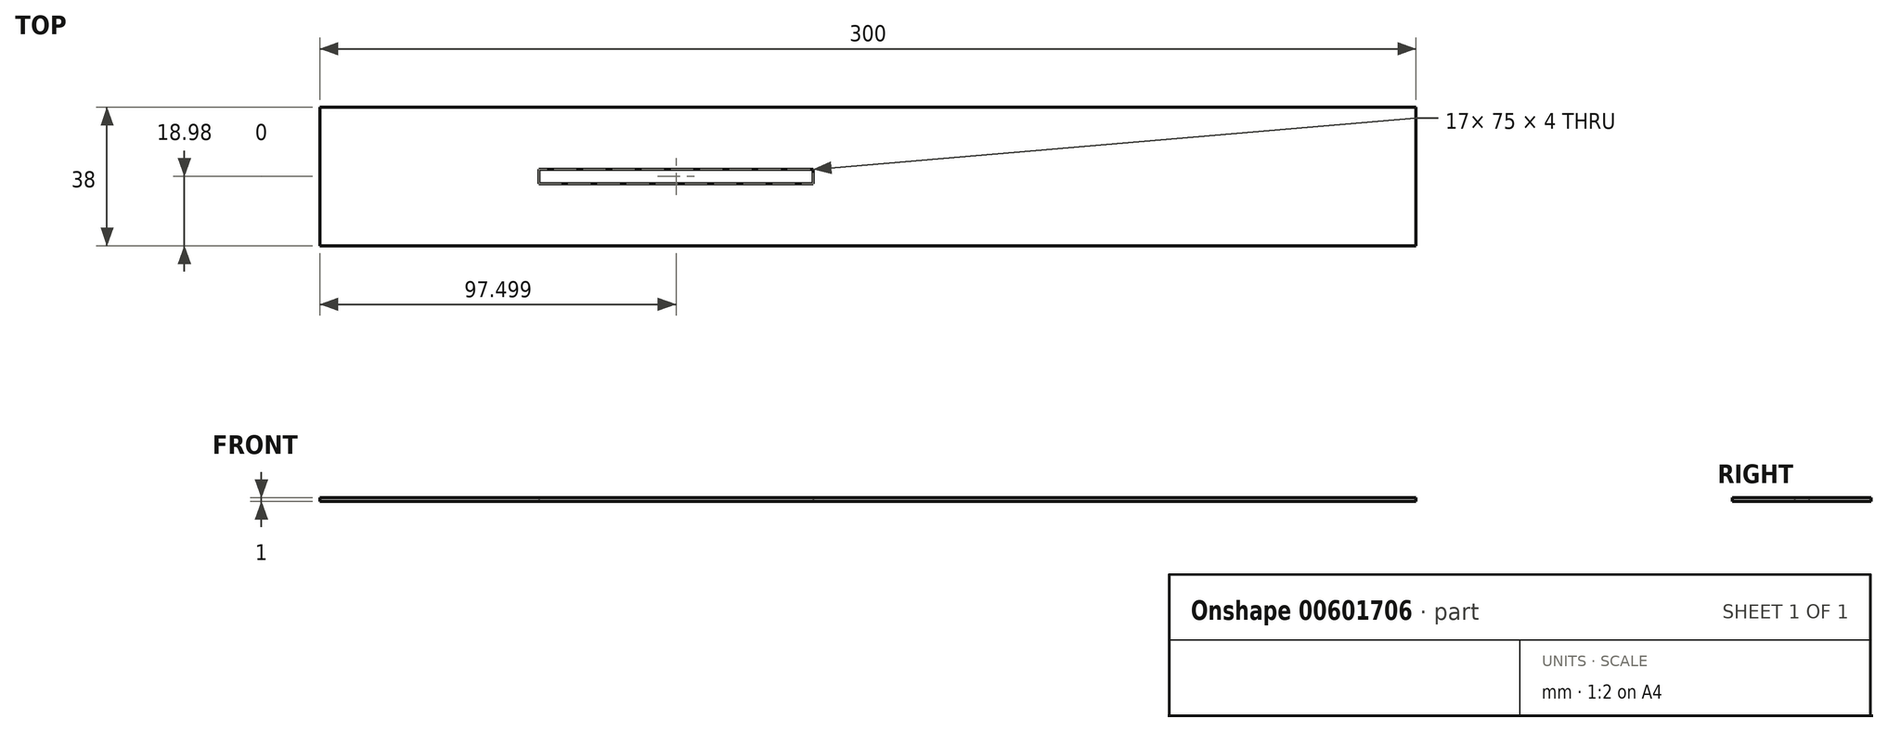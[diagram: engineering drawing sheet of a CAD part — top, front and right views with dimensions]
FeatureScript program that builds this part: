
annotation { "Feature Type Name" : "Feature", "Feature Type Description" : "" }
export const myFeature = defineFeature(function(context is Context, id is Id, definition is map)
    precondition{}
    {
        {
            var Q0;
            Q0=qCreatedBy(makeId("Top.planeOp"),FACE);
            var sketch = newSketch(context, id + "F0", { "sketchPlane" : qUnion([Q0])});
            skLineSegment(sketch, "E0.bottom", {"start": v(-131, 19) * mm, "end": v(169, 19) * mm});
            skLineSegment(sketch, "E0.top", {"start": v(-131, -19) * mm, "end": v(169, -19) * mm});
            skLineSegment(sketch, "E0.left", {"start": v(-131, 19) * mm, "end": v(-131, -19) * mm});
            skLineSegment(sketch, "E0.right", {"start": v(169, 19) * mm, "end": v(169, -19) * mm});
            skLineSegment(sketch, "E1.bottom", {"start": v(-71, 1.98) * mm, "end": v(4, 1.98) * mm});
            skLineSegment(sketch, "E1.top", {"start": v(-71, -2.02) * mm, "end": v(4, -2.02) * mm});
            skLineSegment(sketch, "E1.left", {"start": v(-71, 1.98) * mm, "end": v(-71, -2.02) * mm});
            skLineSegment(sketch, "E1.right", {"start": v(4, 1.98) * mm, "end": v(4, -2.02) * mm});
            skSolve(sketch);
        }
        {
            var Q0;
            Q0=makeQuery(id+"F0.imprint","IMPRINT",FACE,{"disambiguationData":[TD([[makeQuery(id+"F0.imprint","IMPRINT",EDGE,{"derivedFrom":sQuery(id+"F0.wireOp",EDGE,"E0.bottom")}),-1.0]])]});
            extrude(context, id + "F1", {"entities" : qUnion([Q0]), "depth" : 1 * mm, "offsetDistance" : 25 * mm});
        }
    });
